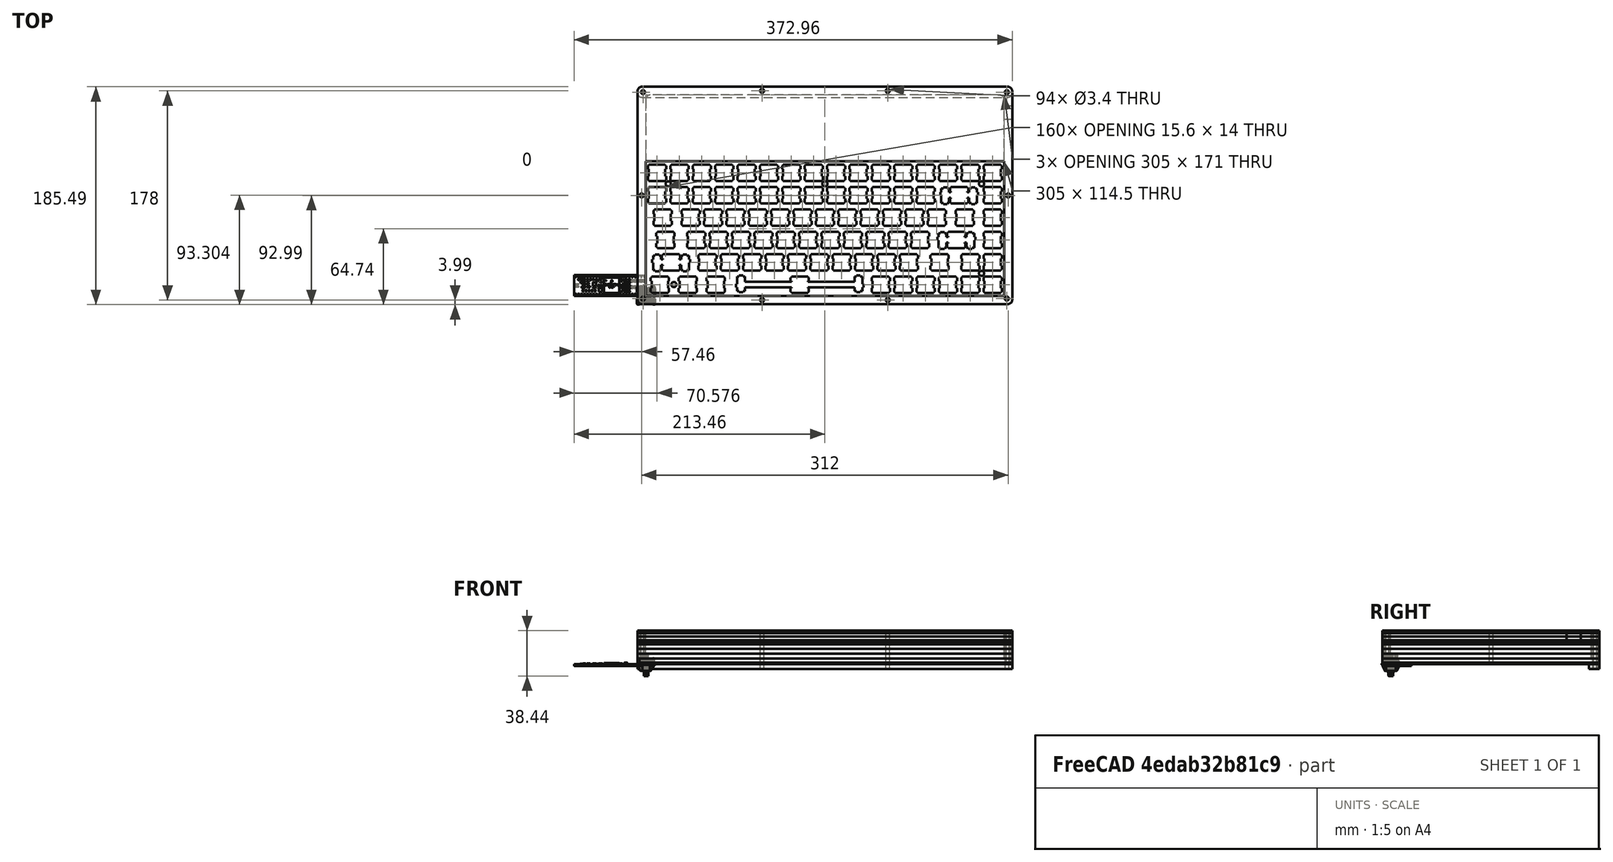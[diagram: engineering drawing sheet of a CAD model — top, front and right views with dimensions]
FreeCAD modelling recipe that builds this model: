
FCSTD DOCUMENT  (FreeCAD 0.19R24291 (Git))
Label: case
License: All rights reserved
LicenseURL: http://en.wikipedia.org/wiki/All_rights_reserved
objects: Part::Feature×93, Part::Extrusion×23, Part::Cut×23, Part::Part2DObjectPython×9, App::DocumentObjectGroup×7, Part::Cylinder×6, Part::Fillet×5, Part::MultiFuse×3, App::Part×2, App::VRMLObject×1, Part::Compound×1, Part::Refine×1
note: 164 computed .brp shape members not serialized (recipe doc carries the construction recipe); baked Part::Feature solids carry a one-line shape summary decoded from their .brp

FEATURE [Part::Part2DObjectPython] Rectangle  label="pcb_hole"  # Draft 2D object (typed FeaturePython)
  ChamferSize = 0
  Columns = 1
  FilletRadius = 0
  Height = 171
  Length = 305
  MakeFace = false
  Rows = 1
FEATURE [Part::Part2DObjectPython] Rectangle001  label="outside_edge"  # Draft 2D object (typed FeaturePython)
  ChamferSize = 0
  Columns = 1
  FilletRadius = 3.81
  Height = 185
  Length = 319
  MakeFace = false
  Placement = pos=(-7,-7,0) rot=(0,0,1;0rad)
  Rows = 1
FEATURE [App::VRMLObject] _0Key  label="PCB001"
  Placement = pos=(-39.6,211.23,14.63) rot=(0,0,1;0rad)
FEATURE [Part::Extrusion] Extrude  label="layer_bottom"
  Base = -> Rectangle001
  Dir = (0,0,1)
  DirMode = 2
  FaceMakerClass = Part::FaceMakerBullseye
  LengthFwd = 5
  LengthRev = 0
  Solid = true
  Symmetric = false
FEATURE [Part::Extrusion] Extrude001  label="ext_pcb_hole"
  Base = -> Rectangle
  Dir = (0,0,1)
  DirMode = 2
  FaceMakerClass = Part::FaceMakerBullseye
  LengthFwd = 4
  LengthRev = 0
  Solid = true
  Symmetric = false
FEATURE [Part::Extrusion] Extrude002  label="ext_outside_edge"
  Base = -> Rectangle001
  Dir = (0,0,1)
  DirMode = 2
  FaceMakerClass = Part::FaceMakerBullseye
  LengthFwd = 4
  LengthRev = 0
  Solid = true
  Symmetric = false
FEATURE [Part::Feature] Part__Feature  label="MX_DOWN"
  Placement = pos=(0.307087,0.307087,-0.34252) rot=(0,0,1;0rad)
  shape: bbox 15.6 x 15.6 x 12.5 mm, 315 faces (baked)
FEATURE [Part::Feature] Part__Feature001  label="MX_UP"
  Placement = pos=(0.307087,0.307087,-5.74252) rot=(0,0,1;0rad)
  shape: bbox 14.7 x 14.7 x 10.05 mm, 224 faces (baked)
FEATURE [Part::Feature] Part__Feature002  label="UP_MX"
  Placement = pos=(3.15709,0.307087,0.45748) rot=(0.57735,0.57735,-0.57735;4.18879rad)
  shape: bbox 5.7 x 8.9 x 12.41 mm, 79 faces (baked)
FEATURE [Part::Feature] Part__Feature003  label="MX_PIN"
  Placement = pos=(-2.59291,4.00709,8.45748) rot=(0.57735,-0.57735,0.57735;4.18879rad)
  shape: bbox 3.189 x 9.805 x 13.16 mm, 187 faces, 2 solids (baked)
FEATURE [Part::Feature] Part__Feature004  label="MX_SPRING"
  Placement = pos=(0.307087,0.307087,6.75748) rot=(0,0,1;0rad)
  shape: bbox 3.277 x 3.277 x 11.32 mm, 14 faces (baked)
FEATURE [Part::Feature] Part__Feature005  label="MX_CLICK"
  Placement = pos=(-2.14619,-4.14291,2.15226) rot=(-1,0,0;1.5708rad)
  shape: bbox 6.847 x 8.901 x 3.85 mm, 123 faces (baked)
FEATURE [App::Part] ASM_MX_ASM
  Group = -> [Part__Feature,Part__Feature001,Part__Feature002,Part__Feature003,Part__Feature004,Part__Feature005]
  Origin = -> Origin
  Placement = pos=(9.3,104.56,20.96) rot=(0.707107,0.707107,0;3.14159rad)
FEATURE [Part::Part2DObjectPython] Rectangle002  label="plate_outside"  # Draft 2D object (typed FeaturePython)
  ChamferSize = 0
  Columns = 1
  FilletRadius = 3.81
  Height = 185
  Length = 319
  MakeFace = false
  Placement = pos=(-7,-7,0) rot=(0,0,1;0rad)
  Rows = 1
FEATURE [Part::Feature] Polyline001 .. Polyline006  x6 (patterned run collapsed; names and placements below)
  shape: bbox 15.6 x 14 x 2e-07 mm, 0 faces, 0 solids (baked)
  placements: all 6 at pos=(-4.91,119.39,0) rot=(0,0,1;0rad)
FEATURE [Part::Feature] Polyline007
  Placement = pos=(-4.91,119.39,0) rot=(0,0,1;0rad)
  shape: bbox 108.4 x 14.75 x 2e-07 mm, 0 faces, 0 solids (baked)
FEATURE [Part::Feature] Polyline008
  Placement = pos=(-4.91,119.39,0) rot=(0,0,1;0rad)
  shape: bbox 15.6 x 14 x 2e-07 mm, 0 faces, 0 solids (baked)
FEATURE [Part::Feature] Polyline009
  Placement = pos=(-4.91,119.39,0) rot=(0,0,1;0rad)
  shape: bbox 15.6 x 14 x 2e-07 mm, 0 faces, 0 solids (baked)
FEATURE [Part::Feature] Polyline010
  Placement = pos=(-4.91,119.39,0) rot=(0,0,1;0rad)
  shape: bbox 15.6 x 14 x 2e-07 mm, 0 faces, 0 solids (baked)
FEATURE [Part::Feature] Polyline011
  Placement = pos=(-4.91,119.39,0) rot=(0,0,1;0rad)
  shape: bbox 32.2 x 14.75 x 2e-07 mm, 0 faces, 0 solids (baked)
FEATURE [Part::Feature] Polyline012 .. Polyline024  x13 (patterned run collapsed; names and placements below)
  shape: bbox 15.6 x 14 x 2e-07 mm, 0 faces, 0 solids (baked)
  placements: all 13 at pos=(-4.91,119.39,0) rot=(0,0,1;0rad)
FEATURE [Part::Feature] Polyline025
  Placement = pos=(-4.91,119.39,0) rot=(0,0,1;0rad)
  shape: bbox 32.2 x 14.75 x 2e-07 mm, 0 faces, 0 solids (baked)
FEATURE [Part::Feature] Polyline026 .. Polyline053  x28 (patterned run collapsed; names and placements below)
  shape: bbox 15.6 x 14 x 2e-07 mm, 0 faces, 0 solids (baked)
  placements: all 28 at pos=(-4.91,119.39,0) rot=(0,0,1;0rad)
FEATURE [Part::Feature] Polyline054
  Placement = pos=(-4.91,119.39,0) rot=(0,0,1;0rad)
  shape: bbox 32.2 x 14.75 x 2e-07 mm, 0 faces, 0 solids (baked)
FEATURE [Part::Feature] Polyline055 .. Polyline084  x30 (patterned run collapsed; names and placements below)
  shape: bbox 15.6 x 14 x 2e-07 mm, 0 faces, 0 solids (baked)
  placements: all 30 at pos=(-4.91,119.39,0) rot=(0,0,1;0rad)
FEATURE [Part::Compound] Compound
  Links = -> [Polyline001,Polyline018,Polyline011,Polyline012,Polyline013,Polyline015,Polyline016,Polyline017,Polyline006,Polyline008,Polyline002,Polyline014,Polyline004,Polyline005,Polyline007,Polyline009,Polyline010,Polyline003,Polyline034,Polyline037,Polyline033,Polyline038,Polyline021,Polyline022,Polyline027,Polyline030,Polyline039,Polyline040,Polyline041,Polyline023,Polyline019,Polyline036,Polyline031,+51 more]
FEATURE [App::DocumentObjectGroup] Group004  label="import"
  Group = -> [Compound]
FEATURE [Part::Extrusion] Extrude003
  Base = -> Rectangle002
  Dir = (0,0,1)
  DirMode = 2
  FaceMakerClass = Part::FaceMakerBullseye
  LengthFwd = 1.5
  LengthRev = 0
  Solid = true
  Symmetric = false
FEATURE [Part::Extrusion] Extrude004
  Base = -> Compound
  Dir = (0,0,1)
  DirMode = 2
  FaceMakerClass = Part::FaceMakerBullseye
  LengthFwd = 1.5
  LengthRev = 0
  Solid = true
  Symmetric = false
FEATURE [Part::Cut] Cut004  label="layer_plate_ref"
  Base = -> Extrude003
  Tool = -> Extrude004
FEATURE [Part::Part2DObjectPython] Rectangle003  label="cutout"  # Draft 2D object (typed FeaturePython)
  ChamferSize = 0
  Columns = 1
  FilletRadius = 0
  Height = 56.5
  Length = 305
  MakeFace = false
  Placement = pos=(0,114.5,0) rot=(0,0,1;0rad)
  Rows = 1
FEATURE [Part::Extrusion] Extrude005  label="cutout_ext"
  Base = -> Rectangle003
  Dir = (0,0,1)
  DirMode = 2
  FaceMakerClass = Part::FaceMakerBullseye
  LengthFwd = 4
  LengthRev = 0
  Solid = true
  Symmetric = false
FEATURE [Part::Fillet] Fillet
  Base = -> Extrude005
  Edges = 2 edges r=3.81: [Edge5,Edge8]
FEATURE [Part::Cut] Cut005  label="layer_switch_ref"
  Base = -> Cut004
  Tool = -> Fillet
FEATURE [App::DocumentObjectGroup] Group003  label="plate"
  Group = -> [Group004,Cut005]
FEATURE [Part::Cut] Cut006  label="layer_switch"
  Base = -> Cut004
  Placement = pos=(0,0,19) rot=(0,0,1;0rad)
  Tool = -> Fillet
FEATURE [Part::Extrusion] Extrude006  label="ex_out_3mm"
  Base = -> Rectangle001
  Dir = (0,0,1)
  DirMode = 2
  FaceMakerClass = Part::FaceMakerBullseye
  LengthFwd = 3
  LengthRev = 0
  Solid = true
  Symmetric = false
FEATURE [Part::Extrusion] Extrude007  label="ext_pcb_3mm"
  Base = -> Rectangle
  Dir = (0,0,1)
  DirMode = 2
  FaceMakerClass = Part::FaceMakerBullseye
  LengthFwd = 3
  LengthRev = 0
  Solid = true
  Symmetric = false
FEATURE [Part::Feature] Part__Feature006  label="Teensy 3_5"
  shape: bbox 60.96 x 17.78 x 3.062 mm, 1427 faces, 74 solids (baked)
FEATURE [Part::Feature] Part__Feature007  label="DM3D-SF"
  Placement = pos=(-9.15759,6.51929,0) rot=(0,0,1;1.5708rad)
  shape: bbox 11.46 x 11.96 x 1.563 mm, 957 faces, 0 solids (baked)
FEATURE [Part::Feature] Part__Feature008  label="473460001"
  Placement = pos=(-58.5674,8.82223,1.23741) rot=(0.57735,-0.57735,-0.57735;2.0944rad)
  shape: bbox 5.43 x 7.98 x 2.94 mm, 408 faces, 0 solids (baked)
FEATURE [App::Part] Teensy_3_6  label="Teensy 3_6"
  Group = -> [Part__Feature006,Part__Feature007,Part__Feature008]
  Origin = -> Origin001
  Placement = pos=(221.71,165.2,18.5) rot=(0,0,1;3.14159rad)
FEATURE [App::DocumentObjectGroup] Group  label="ref"
  Group = -> [_0Key,ASM_MX_ASM,Teensy_3_6]
FEATURE [Part::Part2DObjectPython] Circle  label="hole_corner"  # Draft 2D object (typed FeaturePython)
  Area = 0
  FirstAngle = 0
  LastAngle = 0
  MakeFace = false
  Placement = pos=(-2.3,-2.3,0) rot=(0,0,1;0rad)
  Radius = 1.7
FEATURE [Part::Part2DObjectPython] Circle001  label="hole_no"  # Draft 2D object (typed FeaturePython)
  Area = 0
  FirstAngle = 0
  LastAngle = 0
  MakeFace = false
  Placement = pos=(99,-3.5,0) rot=(0,0,1;0rad)
  Radius = 1.7
FEATURE [Part::Extrusion] Extrude009  label="b1"
  Base = -> Circle
  Dir = (0,0,1)
  DirMode = 2
  FaceMakerClass = Part::FaceMakerBullseye
  LengthFwd = 40
  LengthRev = 0
  Solid = true
  Symmetric = false
FEATURE [Part::Extrusion] Extrude010  label="b2"
  Base = -> Circle001
  Dir = (0,0,1)
  DirMode = 2
  FaceMakerClass = Part::FaceMakerBullseye
  LengthFwd = 40
  LengthRev = 0
  Solid = true
  Symmetric = false
FEATURE [Part::Extrusion] Extrude011  label="b3"
  Base = -> Circle001
  Dir = (0,0,1)
  DirMode = 2
  FaceMakerClass = Part::FaceMakerBullseye
  LengthFwd = 40
  LengthRev = 0
  Placement = pos=(107,0,0) rot=(0,0,1;0rad)
  Solid = true
  Symmetric = false
FEATURE [Part::Extrusion] Extrude012  label="b4"
  Base = -> Circle
  Dir = (0,0,1)
  DirMode = 2
  FaceMakerClass = Part::FaceMakerBullseye
  LengthFwd = 40
  LengthRev = 0
  Placement = pos=(309.7,0,0) rot=(0,0,1;0rad)
  Solid = true
  Symmetric = false
FEATURE [Part::Extrusion] Extrude013  label="t1"
  Base = -> Circle
  Dir = (0,0,1)
  DirMode = 2
  FaceMakerClass = Part::FaceMakerBullseye
  LengthFwd = 40
  LengthRev = 0
  Placement = pos=(0,175.7,-10) rot=(0,0,1;0rad)
  Solid = true
  Symmetric = false
FEATURE [Part::Extrusion] Extrude014  label="t2"
  Base = -> Circle001
  Dir = (0,0,1)
  DirMode = 2
  FaceMakerClass = Part::FaceMakerBullseye
  LengthFwd = 50
  LengthRev = 0
  Placement = pos=(0,178,-10) rot=(0,0,1;0rad)
  Solid = true
  Symmetric = false
FEATURE [Part::Extrusion] Extrude015  label="t3"
  Base = -> Circle001
  Dir = (0,0,1)
  DirMode = 2
  FaceMakerClass = Part::FaceMakerBullseye
  LengthFwd = 50
  LengthRev = 0
  Placement = pos=(107,178,-10) rot=(0,0,1;0rad)
  Solid = true
  Symmetric = false
FEATURE [Part::Extrusion] Extrude016  label="t4"
  Base = -> Circle
  Dir = (0,0,1)
  DirMode = 2
  FaceMakerClass = Part::FaceMakerBullseye
  LengthFwd = 50
  LengthRev = 0
  Placement = pos=(309.7,175.7,-10) rot=(0,0,1;0rad)
  Solid = true
  Symmetric = false
FEATURE [Part::Part2DObjectPython] Circle002  label="hole_mid"  # Draft 2D object (typed FeaturePython)
  Area = 0
  FirstAngle = 0
  LastAngle = 0
  MakeFace = false
  Placement = pos=(-3.5,85.5,0) rot=(0,0,1;0rad)
  Radius = 1.7
FEATURE [Part::Extrusion] Extrude017  label="m1"
  Base = -> Circle002
  Dir = (0,0,1)
  DirMode = 2
  FaceMakerClass = Part::FaceMakerBullseye
  LengthFwd = 40
  LengthRev = 0
  Solid = true
  Symmetric = false
FEATURE [Part::Extrusion] Extrude018  label="m2"
  Base = -> Circle002
  Dir = (0,0,1)
  DirMode = 2
  FaceMakerClass = Part::FaceMakerBullseye
  LengthFwd = 40
  LengthRev = 0
  Placement = pos=(312,0,0) rot=(0,0,1;0rad)
  Solid = true
  Symmetric = false
FEATURE [Part::MultiFuse] Fusion002  label="grp_holes"
  Shapes = -> [Extrude009,Extrude010,Extrude011,Extrude012,Extrude013,Extrude014,Extrude015,Extrude016,Extrude017,Extrude018]
FEATURE [Part::Cut] Cut009  label="hlayer_bottom"
  Base = -> Extrude
  Tool = -> Fusion002
FEATURE [Part::Cut] Cut013  label="hlayer_switch"
  Base = -> Cut006
  Tool = -> Fusion002
FEATURE [Part::Part2DObjectPython] Rectangle004  label="usb_hole"  # Draft 2D object (typed FeaturePython)
  Area = 0
  ChamferSize = 0
  Columns = 1
  FilletRadius = 0
  Height = 12
  Length = 7
  MakeFace = false
  Placement = pos=(305,150,0) rot=(0,0,1;0rad)
  Rows = 1
FEATURE [Part::Extrusion] Extrude019  label="ext_usb_hole"
  Base = -> Rectangle004
  Dir = (0,0,1)
  DirMode = 2
  FaceMakerClass = Part::FaceMakerBullseye
  LengthFwd = 40
  LengthRev = 0
  Solid = true
  Symmetric = false
FEATURE [Part::Cut] Cut016  label="hlayer_switch_usb"
  Base = -> Cut013
  Tool = -> Extrude019
FEATURE [Part::Part2DObjectPython] Rectangle005  label="foot"  # Draft 2D object (typed FeaturePython)
  Area = 0
  ChamferSize = 0
  Columns = 1
  FilletRadius = 3.81
  Height = 9
  Length = 319
  MakeFace = false
  Placement = pos=(-7,169,0) rot=(0,0,1;0rad)
  Rows = 1
FEATURE [App::DocumentObjectGroup] Group001  label="drawings"
  Group = -> [Rectangle,Rectangle001,Rectangle003,Circle,Circle001,Circle002,Rectangle004,Rectangle005]
FEATURE [Part::Extrusion] Extrude020  label="ext_foot"
  Base = -> Rectangle005
  Dir = (0,0,-1)
  DirMode = 0
  FaceMakerClass = Part::FaceMakerBullseye
  LengthFwd = 4
  LengthRev = 0
  Solid = true
  Symmetric = false
FEATURE [Part::Cut] Cut018  label="hlayer_foot"
  Base = -> Extrude020
  Tool = -> Fusion002
FEATURE [Part::Fillet] Fillet002  label="ext_pcb_hole_fillet"
  Base = -> Extrude001
  Edges = 2 edges r=3.81: [Edge5,Edge8]
FEATURE [Part::Cut] Cut  label="layer_closed_1"
  Base = -> Extrude002
  Placement = pos=(0,0,5) rot=(0,0,1;0rad)
  Tool = -> Fillet002
FEATURE [Part::Cut] Cut001  label="layer_closed_2"
  Base = -> Extrude002
  Placement = pos=(0,0,9) rot=(0,0,1;0rad)
  Tool = -> Fillet002
FEATURE [Part::Cut] Cut002  label="layer_closed_3"
  Base = -> Extrude002
  Placement = pos=(0,0,13) rot=(0,0,1;0rad)
  Tool = -> Fillet002
FEATURE [Part::Cut] Cut010  label="hlayer_closed_1"
  Base = -> Cut
  Tool = -> Fusion002
FEATURE [Part::Cut] Cut011  label="hlayer_closed_2"
  Base = -> Cut001
  Tool = -> Fusion002
FEATURE [Part::Cut] Cut012  label="hlayer_closed_3"
  Base = -> Cut002
  Tool = -> Fusion002
FEATURE [Part::Fillet] Fillet003  label="ext_pcb_3mm_fillet"
  Base = -> Extrude007
  Edges = 2 edges r=3.81: [Edge5,Edge8]
FEATURE [Part::Cut] Cut007  label="layer_top_1"
  Base = -> Extrude006
  Placement = pos=(0,0,20.5) rot=(0,0,1;0rad)
  Tool = -> Fillet003
FEATURE [Part::Cut] Cut014  label="hlayer_top_1"
  Base = -> Cut007
  Tool = -> Fusion002
FEATURE [Part::Cut] Cut017  label="hlayer_top_1_usb"
  Base = -> Cut014
  Tool = -> Extrude019
FEATURE [Part::Extrusion] Extrude023  label="ex_out_2mm"
  Base = -> Rectangle001
  Dir = (0,0,1)
  DirMode = 2
  FaceMakerClass = Part::FaceMakerBullseye
  LengthFwd = 2
  LengthRev = 0
  Solid = true
  Symmetric = false
FEATURE [Part::Extrusion] Extrude024  label="ext_pcb_2mm"
  Base = -> Rectangle
  Dir = (0,0,1)
  DirMode = 2
  FaceMakerClass = Part::FaceMakerBullseye
  LengthFwd = 2
  LengthRev = 0
  Solid = true
  Symmetric = false
FEATURE [Part::Fillet] Fillet005  label="ext_pcb_2mm_fillet"
  Base = -> Extrude024
  Edges = 2 edges r=3.81: [Edge5,Edge8]
FEATURE [Part::Cut] Cut008  label="layer_top_2"
  Base = -> Extrude023
  Placement = pos=(0,0,24.5) rot=(0,0,1;0rad)
  Tool = -> Fillet005
FEATURE [Part::Extrusion] Extrude025  label="ext_cutout_2mm"
  Base = -> Rectangle003
  Dir = (0,0,1)
  DirMode = 2
  FaceMakerClass = Part::FaceMakerBullseye
  LengthFwd = 2
  LengthRev = 0
  Solid = true
  Symmetric = false
FEATURE [Part::Fillet] Fillet006  label="fil_cutout_2mm"
  Base = -> Extrude025
  Edges = 2 edges r=3.81: [Edge5,Edge8]
  Placement = pos=(0,0,24.5) rot=(0,0,1;0rad)
FEATURE [Part::MultiFuse] Fusion  label="layer_top_2_raw"
  Shapes = -> [Fillet006,Cut008]
FEATURE [Part::Refine] Fusion001  label="layer_top_2_ref"
  Source = -> Fusion
FEATURE [Part::Cut] Cut015  label="hlayer_top_3"
  Base = -> Fusion001
  Placement = pos=(0,0,2) rot=(0,0,1;0rad)
  Tool = -> Fusion002
FEATURE [Part::Cut] Cut019  label="hlayer_top_2_usb"
  Base = -> Cut014
  Placement = pos=(0,0,3) rot=(0,0,1;0rad)
  Tool = -> Extrude019
FEATURE [Part::Cut] Cut020  label="layer_switch_spacer"
  Base = -> Extrude023
  Placement = pos=(0,0,17) rot=(0,0,1;0rad)
  Tool = -> Fillet005
FEATURE [Part::Cut] Cut022  label="hlayer_switch_spacer"
  Base = -> Cut020
  Tool = -> Fusion002
FEATURE [Part::Cut] Cut021  label="hlayer_switch_spacer_usb"
  Base = -> Cut022
  Tool = -> Extrude019
FEATURE [Part::Cylinder] Cylinder  label="sh_bl"
  Angle = 360
  AttacherType = Attacher::AttachEngine3D
  Height = 40
  Placement = pos=(23.91,9.63,0) rot=(0,0,1;0rad)
  Radius = 2.2
FEATURE [Part::Cylinder] Cylinder001  label="sh_bm"
  Angle = 360
  AttacherType = Attacher::AttachEngine3D
  Height = 40
  Placement = pos=(152.5,9.63,0) rot=(0,0,1;0rad)
  Radius = 2.2
FEATURE [Part::Cylinder] Cylinder002  label="sh_br"
  Angle = 360
  AttacherType = Attacher::AttachEngine3D
  Height = 40
  Placement = pos=(285.85,19.15,0) rot=(0,0,1;0rad)
  Radius = 2.2
FEATURE [Part::Cylinder] Cylinder003  label="sh_tl"
  Angle = 360
  AttacherType = Attacher::AttachEngine3D
  Height = 40
  Placement = pos=(19.15,95.35,0) rot=(0,0,1;0rad)
  Radius = 2.2
FEATURE [Part::Cylinder] Cylinder004  label="sh_tm"
  Angle = 360
  AttacherType = Attacher::AttachEngine3D
  Height = 40
  Placement = pos=(152.5,95.35,0) rot=(0,0,1;0rad)
  Radius = 2.2
FEATURE [Part::Cylinder] Cylinder005  label="sh_tr"
  Angle = 360
  AttacherType = Attacher::AttachEngine3D
  Height = 40
  Placement = pos=(285.85,95.35,0) rot=(0,0,1;0rad)
  Radius = 2.2
FEATURE [Part::MultiFuse] Fusion003  label="plate_holes"
  Shapes = -> [Cylinder,Cylinder001,Cylinder002,Cylinder003,Cylinder004,Cylinder005]
FEATURE [Part::Cut] Cut023  label="hlayer_switch_plate"
  Base = -> Cut016
  Tool = -> Fusion003
FEATURE [App::DocumentObjectGroup] Group008  label="final layers"
  Group = -> [Cut015,Cut019,Cut017,Cut023,Cut021,Cut012,Cut011,Cut010,Cut009,Cut018]
FEATURE [App::DocumentObjectGroup] Group005  label="holes"
  Group = -> [Fusion002]
FEATURE [App::DocumentObjectGroup] Group002  label="case"
  Group = -> [Fusion,Group005,Group008]
